AUTODESK INVENTOR PART (.ipt)
format: ipt  version: 2015 (Build 190159000, 159)  size: 618,496 bytes
history: native  units: mm (DEFAULTED — no unit token found)
features: other x3, extrude x2, fillet x1, pattern_circular x1
ambient origin geometry x8: Origin, YZ Plane, XZ Plane, XY Plane, X Axis, Y Axis, Z Axis, Center Point
bodies: Solid1 (feature_tree)
feature tree (7):
  other  "皮带轮草图"
  extrude  "基础实体"  Depth=194.041707mm
  extrude  "齿"  Depth=0.6858mm
  fillet  "Fillet"  Radius=3.048mm
  pattern_circular  "Teeth"  [2 undecoded]
  other  "左侧凸缘"
  other  "右侧凸缘"
note: 2 required parameter values undecoded (feature->parameter linkage not recoverable at this tier; creation-order binding heuristic only, values carry confidence <= 0.55)
